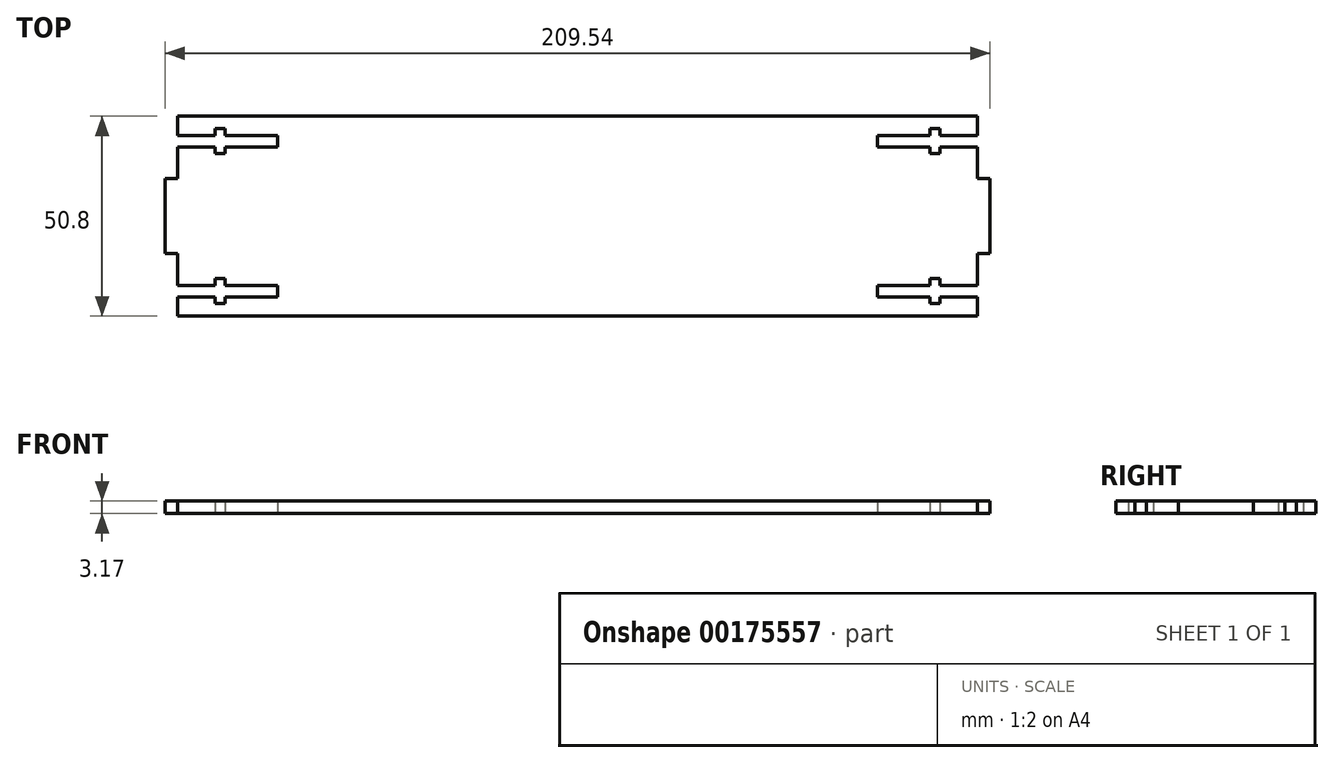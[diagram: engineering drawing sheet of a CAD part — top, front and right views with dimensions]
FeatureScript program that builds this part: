
annotation { "Feature Type Name" : "Feature", "Feature Type Description" : "" }
export const myFeature = defineFeature(function(context is Context, id is Id, definition is map)
    precondition{}
    {
        {
            var Q0;
            Q0=qCreatedBy(makeId("Top.planeOp"),FACE);
            var sketch = newSketch(context, id + "F0", { "sketchPlane" : qUnion([Q0])});
            skLineSegment(sketch, "E0.top", {"start": v(0, 25.4) * mm, "end": v(-101.6, 25.4) * mm});
            skLineSegment(sketch, "E0.left", {"start": v(0, 0) * mm, "end": v(0, 25.4) * mm, "construction": true});
            skLineSegment(sketch, "E0.right", {"start": v(-101.6, 9.53) * mm, "end": v(-101.6, 17.59) * mm});
            skLineSegment(sketch, "E1.bottom", {"start": v(-104.78, 9.53) * mm, "end": v(-101.6, 9.53) * mm});
            skLineSegment(sketch, "E1.right", {"start": v(-104.77, 0) * mm, "end": v(-104.78, 9.53) * mm});
            skPoint(sketch, "E1.middle", {"position": v(-101.6, 0) * mm});
            skPoint(sketch, "E1.top.start.orphan", {"position": v(-98.43, -9.53) * mm});
            skPoint(sketch, "E2.orphan", {"position": v(-104.77, -9.53) * mm});
            skLineSegment(sketch, "E3", {"start": v(0, 0) * mm, "end": v(-104.77, 0) * mm, "construction": true});
            skLineSegment(sketch, "E4.bottom", {"start": v(-76.2, 17.59) * mm, "end": v(-89.53, 17.59) * mm});
            skLineSegment(sketch, "E4.top", {"start": v(-76.2, 20.51) * mm, "end": v(-89.53, 20.51) * mm});
            skLineSegment(sketch, "E4.left", {"start": v(-76.2, 17.59) * mm, "end": v(-76.2, 20.51) * mm});
            skPoint(sketch, "E4.middle", {"position": v(-101.6, 19.05) * mm});
            skPoint(sketch, "E4.right.end.orphan", {"position": v(-127, 20.51) * mm});
            skPoint(sketch, "E5.orphan", {"position": v(-127, 17.59) * mm});
            skLineSegment(sketch, "E6.trimOffspring", {"start": v(-101.6, 20.51) * mm, "end": v(-101.6, 25.4) * mm});
            skLineSegment(sketch, "E7.bottom", {"start": v(-89.53, 22.23) * mm, "end": v(-92.08, 22.23) * mm});
            skLineSegment(sketch, "E7.top", {"start": v(-89.53, 15.88) * mm, "end": v(-92.08, 15.88) * mm});
            skLineSegment(sketch, "E7.left", {"start": v(-89.53, 22.23) * mm, "end": v(-89.53, 20.51) * mm});
            skLineSegment(sketch, "E7.right", {"start": v(-92.08, 22.23) * mm, "end": v(-92.08, 20.51) * mm});
            skLineSegment(sketch, "E8.trimOffspring", {"start": v(-92.08, 20.51) * mm, "end": v(-101.6, 20.51) * mm});
            skLineSegment(sketch, "E9.trimOffspring", {"start": v(-89.53, 17.59) * mm, "end": v(-89.53, 15.88) * mm});
            skLineSegment(sketch, "E10.trimOffspring", {"start": v(-92.08, 17.59) * mm, "end": v(-92.08, 15.88) * mm});
            skLineSegment(sketch, "E11.trimOffspring", {"start": v(-92.08, 17.59) * mm, "end": v(-101.6, 17.59) * mm});
            skLineSegment(sketch, "E12.MirrorCS", {"start": v(92.08, 17.59) * mm, "end": v(92.08, 15.88) * mm});
            skLineSegment(sketch, "E13.MirrorCS", {"start": v(89.53, 22.23) * mm, "end": v(92.08, 22.23) * mm});
            skLineSegment(sketch, "E14.MirrorCS", {"start": v(76.2, 17.59) * mm, "end": v(76.2, 20.51) * mm});
            skLineSegment(sketch, "E15.MirrorCS", {"start": v(104.78, 9.53) * mm, "end": v(101.6, 9.53) * mm});
            skLineSegment(sketch, "E16.MirrorCS", {"start": v(101.6, 20.51) * mm, "end": v(101.6, 25.4) * mm});
            skLineSegment(sketch, "E17.MirrorCS", {"start": v(89.53, 22.23) * mm, "end": v(89.53, 20.51) * mm});
            skLineSegment(sketch, "E18.MirrorCS", {"start": v(89.53, 17.59) * mm, "end": v(89.53, 15.88) * mm});
            skLineSegment(sketch, "E19.MirrorCS", {"start": v(92.08, 22.23) * mm, "end": v(92.08, 20.51) * mm});
            skLineSegment(sketch, "E20.MirrorCS", {"start": v(89.53, 15.88) * mm, "end": v(92.08, 15.88) * mm});
            skPoint(sketch, "E21.MirrorP", {"position": v(98.43, -9.53) * mm});
            skPoint(sketch, "E22.MirrorP", {"position": v(101.6, 0) * mm});
            skLineSegment(sketch, "E23.MirrorCS", {"start": v(76.2, 20.51) * mm, "end": v(89.53, 20.51) * mm});
            skLineSegment(sketch, "E24.MirrorCS", {"start": v(76.2, 17.59) * mm, "end": v(89.53, 17.59) * mm});
            skLineSegment(sketch, "E25.MirrorCS", {"start": v(0, 0) * mm, "end": v(104.77, 0) * mm, "construction": true});
            skPoint(sketch, "E26.MirrorP", {"position": v(101.6, 19.05) * mm});
            skLineSegment(sketch, "E27.MirrorCS", {"start": v(92.08, 17.59) * mm, "end": v(101.6, 17.59) * mm});
            skLineSegment(sketch, "E28.MirrorCS", {"start": v(104.77, 0) * mm, "end": v(104.78, 9.53) * mm});
            skPoint(sketch, "E29.MirrorP", {"position": v(127, 17.59) * mm});
            skPoint(sketch, "E30.MirrorP", {"position": v(104.77, -9.53) * mm});
            skPoint(sketch, "E31.MirrorP", {"position": v(127, 20.51) * mm});
            skLineSegment(sketch, "E32.MirrorCS", {"start": v(92.08, 20.51) * mm, "end": v(101.6, 20.51) * mm});
            skLineSegment(sketch, "E33.MirrorCS", {"start": v(101.6, 9.53) * mm, "end": v(101.6, 17.59) * mm});
            skLineSegment(sketch, "E34.MirrorCS", {"start": v(0, 25.4) * mm, "end": v(101.6, 25.4) * mm});
            skLineSegment(sketch, "E35.MirrorCS", {"start": v(-89.53, -15.88) * mm, "end": v(-92.08, -15.88) * mm});
            skLineSegment(sketch, "E36.MirrorCS", {"start": v(-89.53, -17.59) * mm, "end": v(-89.53, -15.88) * mm});
            skLineSegment(sketch, "E37.MirrorCS", {"start": v(-92.08, -17.59) * mm, "end": v(-92.08, -15.88) * mm});
            skLineSegment(sketch, "E38.MirrorCS", {"start": v(92.08, -22.22) * mm, "end": v(92.08, -20.51) * mm});
            skLineSegment(sketch, "E39.MirrorCS", {"start": v(89.53, -22.22) * mm, "end": v(92.08, -22.22) * mm});
            skLineSegment(sketch, "E40.MirrorCS", {"start": v(92.08, -17.59) * mm, "end": v(92.08, -15.87) * mm});
            skLineSegment(sketch, "E41.MirrorCS", {"start": v(76.2, -17.59) * mm, "end": v(76.2, -20.51) * mm});
            skLineSegment(sketch, "E42.MirrorCS", {"start": v(101.6, -20.51) * mm, "end": v(101.6, -25.4) * mm});
            skLineSegment(sketch, "E43.MirrorCS", {"start": v(89.53, -22.22) * mm, "end": v(89.53, -20.51) * mm});
            skLineSegment(sketch, "E44.MirrorCS", {"start": v(-89.53, -22.23) * mm, "end": v(-89.53, -20.51) * mm});
            skLineSegment(sketch, "E45.MirrorCS", {"start": v(-89.53, -22.23) * mm, "end": v(-92.08, -22.23) * mm});
            skLineSegment(sketch, "E46.MirrorCS", {"start": v(-101.6, -20.51) * mm, "end": v(-101.6, -25.4) * mm});
            skLineSegment(sketch, "E47.MirrorCS", {"start": v(-76.2, -17.59) * mm, "end": v(-76.2, -20.51) * mm});
            skLineSegment(sketch, "E48.MirrorCS", {"start": v(-104.78, -9.53) * mm, "end": v(-101.6, -9.53) * mm});
            skLineSegment(sketch, "E49.MirrorCS", {"start": v(-92.08, -22.23) * mm, "end": v(-92.08, -20.51) * mm});
            skLineSegment(sketch, "E50.MirrorCS", {"start": v(89.53, -15.87) * mm, "end": v(92.08, -15.87) * mm});
            skLineSegment(sketch, "E51.MirrorCS", {"start": v(89.53, -17.59) * mm, "end": v(89.53, -15.87) * mm});
            skLineSegment(sketch, "E52.MirrorCS", {"start": v(104.78, -9.53) * mm, "end": v(101.6, -9.53) * mm});
            skLineSegment(sketch, "E53.MirrorCS", {"start": v(92.08, -20.51) * mm, "end": v(101.6, -20.51) * mm});
            skLineSegment(sketch, "E54.MirrorCS", {"start": v(0, -25.4) * mm, "end": v(101.6, -25.4) * mm});
            skPoint(sketch, "E55.MirrorP", {"position": v(-101.6, -19.05) * mm});
            skPoint(sketch, "E56.MirrorP", {"position": v(-127, -17.59) * mm});
            skLineSegment(sketch, "E57.MirrorCS", {"start": v(104.78, 0) * mm, "end": v(104.78, -9.53) * mm});
            skLineSegment(sketch, "E58.MirrorCS", {"start": v(76.2, -20.51) * mm, "end": v(89.53, -20.51) * mm});
            skLineSegment(sketch, "E59.MirrorCS", {"start": v(-76.2, -20.51) * mm, "end": v(-89.53, -20.51) * mm});
            skLineSegment(sketch, "E60.MirrorCS", {"start": v(-76.2, -17.59) * mm, "end": v(-89.53, -17.59) * mm});
            skLineSegment(sketch, "E61.MirrorCS", {"start": v(-104.77, 0) * mm, "end": v(-104.77, -9.53) * mm});
            skLineSegment(sketch, "E62.MirrorCS", {"start": v(101.6, -9.53) * mm, "end": v(101.6, -17.59) * mm});
            skPoint(sketch, "E63.MirrorP", {"position": v(101.6, -19.05) * mm});
            skLineSegment(sketch, "E64.MirrorCS", {"start": v(92.08, -17.59) * mm, "end": v(101.6, -17.59) * mm});
            skLineSegment(sketch, "E65.MirrorCS", {"start": v(-92.08, -17.59) * mm, "end": v(-101.6, -17.59) * mm});
            skLineSegment(sketch, "E66.MirrorCS", {"start": v(76.2, -17.59) * mm, "end": v(89.53, -17.59) * mm});
            skLineSegment(sketch, "E67.MirrorCS", {"start": v(-101.6, -9.53) * mm, "end": v(-101.6, -17.59) * mm});
            skLineSegment(sketch, "E68.MirrorCS", {"start": v(0, 0) * mm, "end": v(0, -25.4) * mm, "construction": true});
            skPoint(sketch, "E69.MirrorP", {"position": v(-127, -20.51) * mm});
            skLineSegment(sketch, "E70.MirrorCS", {"start": v(-92.08, -20.51) * mm, "end": v(-101.6, -20.51) * mm});
            skLineSegment(sketch, "E71.MirrorCS", {"start": v(0, -25.4) * mm, "end": v(-101.6, -25.4) * mm});
            skSolve(sketch);
        }
        {
            var Q0;
            Q0 = qSketchRegion(id + "F0", true);
            extrude(context, id + "F1", {"entities" : qUnion([Q0]), "depth" : 3.17 * mm});
        }
    });
